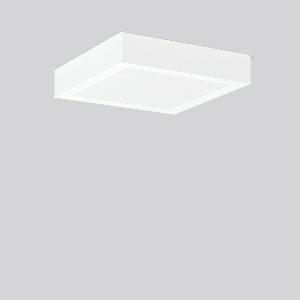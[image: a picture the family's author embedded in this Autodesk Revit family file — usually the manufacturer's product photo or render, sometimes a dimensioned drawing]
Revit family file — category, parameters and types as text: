
# Revit family: toledo_flat_square_a_672277_002_1_07_42c5
name_source: partatom
category: Lighting Fixtures
units: mm (PartAtom-declared; Revit-internal decimal feet)

## family parameters
Cut with Voids When Loaded = No
Host = Face
Light Source = No
Part Type = Normal
Room Calculation Point = No
Round Connector Dimension = Use Diameter
Shared = No

## types (1)
- TOLEDO FLAT square A (1 x LED Modul 840, 2200 lm, 4000)
    Apparent Load = 25 VA
    CIE Flux Codes = 49 80 96 100 100
    Color Rendering = 80
    Color Temperature = 4000
    Default Elevation = 1800 mm
    Description = Series: TOLEDO FLAT square
Ultra thin surface mounted downlight. For escape route illumination. Surface mounted housing: sheet steel, powder-coated. Square cover plate: die-cast aluminium, powder coated. Light guide and diffuser made of non-yellowing PMMA, opal matt. Self-contained system with automatic self-test and feedback via DALI bus, only to RZB DALI monitoring system. 
Colour: white
Length: 300 mm
Width: 300 mm
Height: 58 mm
Weight: 3.96 kg
Operating mode: maintained power mode
Duration time: 3 h
Lamp: LED
Socket: without socket
Colour temperature: 4000K
Colour rendering index (CRI): 80
System power: 25 W
Rated luminous flux: 2200 lm
Luminous flux, emergency: 430 lm
System power, emergency: -
Control gear: Regulated power supply
Protection class: I
Type of protection: IP 40
    Height = 58 mm
    Lamp = 1 x LED Modul 840
    Lamp Light Flux = 2200 lm
    Lamp count = 1
    Length = 300 mm
    Lifetime = 50000 h
    Luminous efficacy = 88 lm/W
    Manufacturer = RZB
    ModVariant = No
    Model = 672277.002.1.07
    Mounting Place = Ceiling
    Mounting Type = Surface mounted
    Number of Poles = 1
    OnlyDefault = Yes
    Power Factor = 1
    Product Name = TOLEDO FLAT square A
    Product group = Surface mounted downlights
    ProductGroupID = 302
    Protection Class = Protection class I
    Protection Degree = IP 40
    RLX_Detail_Level = 1
    RLX_Emergency_Light_Flux = 430 lm
    RLX_Emergency_Type = 3
    RLX_Emergency_Type_DB = Yes
    RlxData = <blob elided: 14109 chars, md5=3902055d>
    Socket = socket
    Standby Power = 0 W
    System Light Flux = 2200 lm
    System Power = 25 W
    Type Comments = Product without accessories
    Type Image = 901554.002.jpg
    URL = http://relux.com
    VarID = ---
    Voltage = 0 V
    Weight = 0.00 kg
    Width = 300 mm

## geometry (parser evidence)
native form markers: Sweep x13
no freeform markers — native parametric forms only
